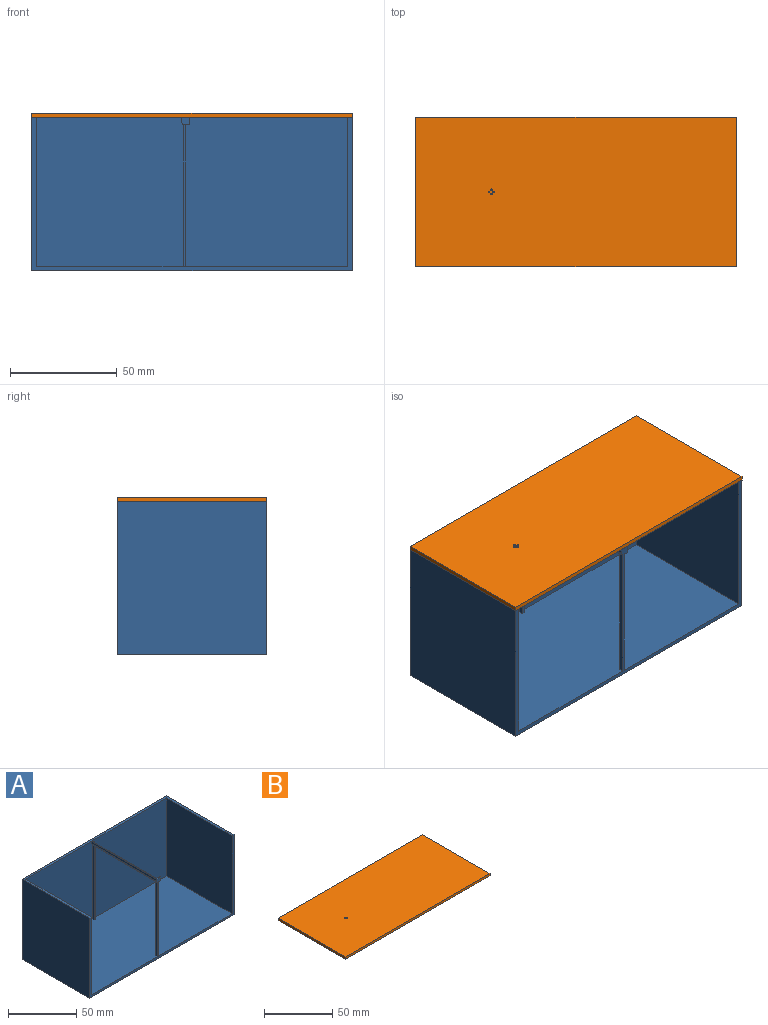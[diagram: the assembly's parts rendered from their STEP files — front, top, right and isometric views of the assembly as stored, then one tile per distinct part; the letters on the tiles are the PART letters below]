
ASSEMBLY  parts=2 mates=1
PART A: 29 faces, bbox 150x70x72 mm
  f0: plane 67x0.5mm, normal (1,0,0), area 33.5mm2, adj f1,f4,f23,f27
  f1: plane 67x1.51mm, normal (0,0,1), area 101mm2, adj f0,f2,f4,f27
  f2: plane 67x0.99mm, normal (0.92,0,0.4), area 72.6mm2, adj f1,f3,f4,f27
  f3: plane 67x2mm, normal (1,0,0), area 134mm2, adj f2,f4,f14,f27
  f4: plane 77.5x70mm, normal (0,-1,0), area 5333.7mm2, adj f0,f1,f2,f3,f5,f11,f14,f19
  f5: plane 66.51x2mm, normal (1,0,0), area 133mm2, adj f4,f7,f11,f23
  f6: plane 66.51x2mm, normal (-1,0,0), area 133mm2, adj f7,f11,f12,f23
  f7: plane 66.51x1mm, normal (0,-1,0), area 66.5mm2, adj f5,f6,f11,f23
  f8: plane 66.51x1mm, normal (0,1,0), area 66.5mm2, adj f9,f10,f11,f23
  f9: plane 66.51x2mm, normal (1,0,0), area 133mm2, adj f8,f11,f22,f23
  f10: plane 66.51x2mm, normal (-1,0,0), area 133mm2, adj f8,f11,f22,f23
  f11: plane 146x68mm, normal (0,0,1), area 9924mm2, adj f4,f5,f6,f7,f8,f9,f10,f12
  f12: plane 70x68.84mm, normal (0,-1,0), area 4816.6mm2, adj f6,f11,f14,f18,f23,f24,f25
  f13: plane 72x70mm, normal (1,0,0), area 5040mm2, adj f14,f16,f17,f20
  f14: plane 150x70mm, normal (0,0,1), area 609.5mm2, adj f3,f4,f12,f13,f15,f16,f17,f18
  f15: plane 72x70mm, normal (-1,0,0), area 5040mm2, adj f14,f16,f17,f20
  f16: plane 150x72mm, normal (0,1,0), area 10799.2mm2, adj f13,f14,f15,f20,f21
  f17: plane 150.01x72.01mm, normal (0,-1,0), area 580mm2, adj f11,f13,f14,f15,f18,f19,f20,f22
  f18: plane 70x68mm, normal (1,0,0), area 4760mm2, adj f11,f12,f14,f17
  f19: plane 70x68mm, normal (-1,0,0), area 4760mm2, adj f4,f11,f14,f17
  f20: plane 150x70mm, normal (0,0,-1), area 10500mm2, adj f13,f15,f16,f17
  f21: cylinder r=0.5mm len=2mm, axis (0,-1,0), area 6.3mm2, adj f4,f16
  f22: plane 66.81x1.01mm, normal (0,-1,0), area 66.8mm2, adj f9,f10,f17,f26
  f23: plane 68x3.35mm, normal (0,0,-1), area 119.3mm2, adj f0,f4,f5,f6,f7,f8,f9,f10
  f24: plane 68x1.49mm, normal (-0.92,0,-0.4), area 110.7mm2, adj f12,f23,f25,f26
  f25: plane 68x2mm, normal (-1,0,0), area 136mm2, adj f12,f14,f24,f26
  f26: plane 4.01x3.5mm, normal (0,-1,0), area 13.2mm2, adj f14,f22,f23,f24,f25,f28
  f27: plane 3.5x3.49mm, normal (0,1,0), area 11mm2, adj f0,f1,f2,f3,f14,f23,f28
  f28: plane 3.49x1mm, normal (1,0,0), area 3.5mm2, adj f14,f23,f26,f27
PART B: 10 faces, bbox 150x70x2 mm
  f0: plane 70x2mm, normal (1,0,0), area 140mm2, adj f1,f3,f4,f5
  f1: plane 150x2mm, normal (0,1,0), area 300mm2, adj f0,f2,f4,f5
  f2: plane 70x2mm, normal (-1,0,0), area 140mm2, adj f1,f3,f4,f5
  f3: plane 150x2mm, normal (0,-1,0), area 300mm2, adj f0,f2,f4,f5
  f4: plane 150x70mm, normal (0,0,1), area 10498.5mm2, adj f0,f1,f2,f3,f6,f7,f8,f9
  f5: plane 150x70mm, normal (0,0,-1), area 10498.5mm2, adj f0,f1,f2,f3,f6,f7,f8,f9
  f6: cylinder r=0.35mm len=2mm, axis (0,0,1), area 4.4mm2, adj f4,f5
  f7: cylinder r=0.35mm len=2mm, axis (0,0,1), area 4.4mm2, adj f4,f5
  f8: cylinder r=0.35mm len=2mm, axis (0,0,1), area 4.4mm2, adj f4,f5
  f9: cylinder r=0.35mm len=2mm, axis (0,0,1), area 4.4mm2, adj f4,f5
PLACE A t=(-106.85,5.82,15.63)mm
PLACE B t=(-109,-29.18,50.63)mm
MATE planar A.f14 <-> B.f5  axis (0,0,1) through (-31.85,5.82,50.63)mm
